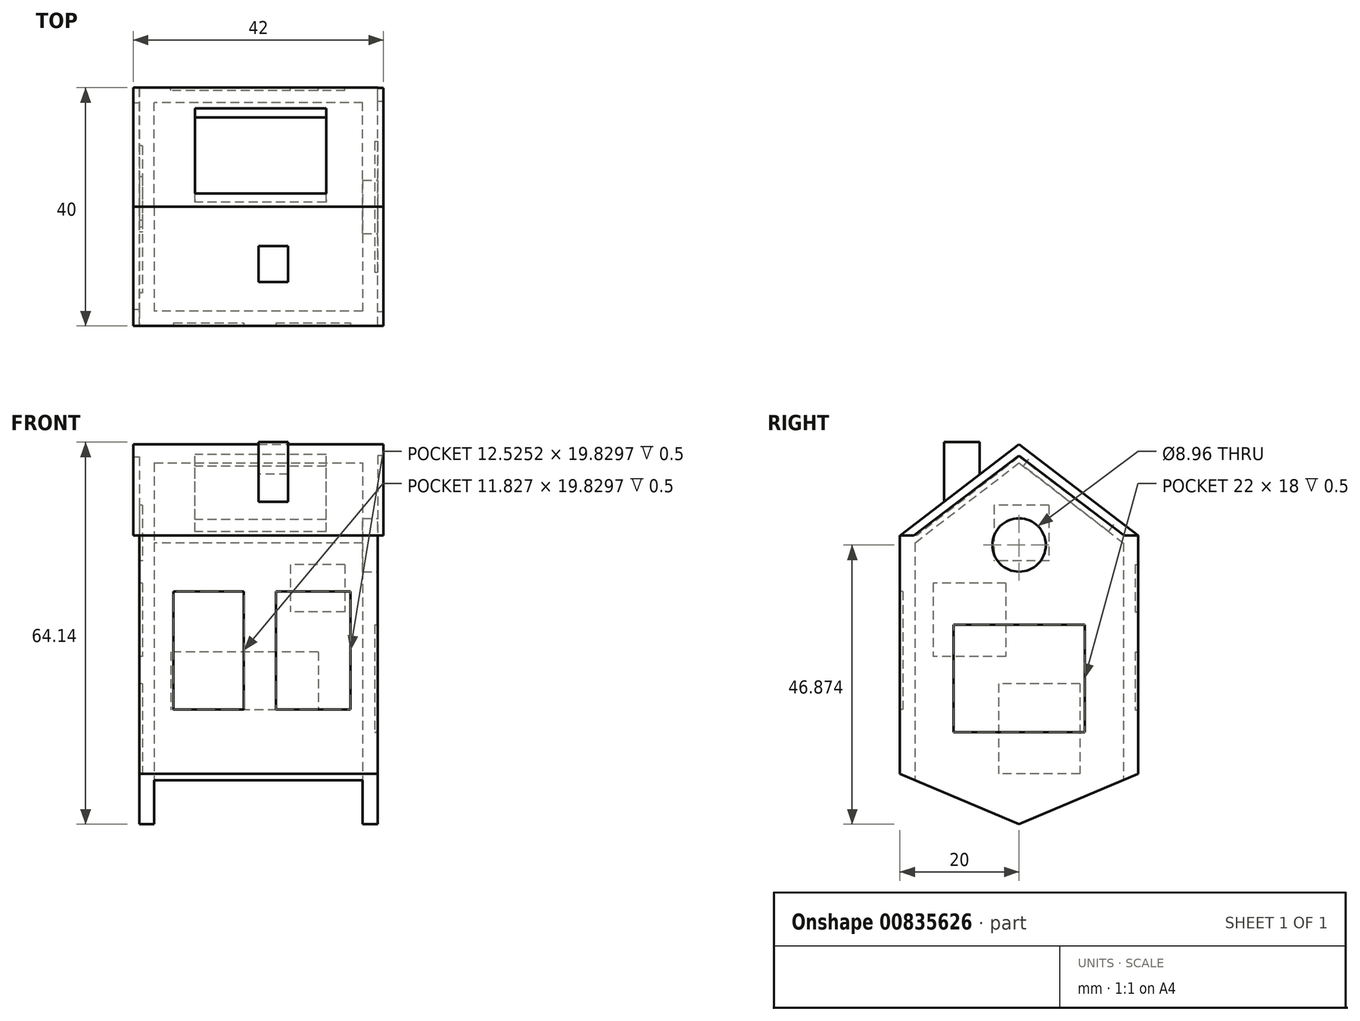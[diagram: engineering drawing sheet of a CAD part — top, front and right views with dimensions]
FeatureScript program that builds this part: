
annotation { "Feature Type Name" : "Feature", "Feature Type Description" : "" }
export const myFeature = defineFeature(function(context is Context, id is Id, definition is map)
    precondition{}
    {
        {
            assignVariable(context, id + "F0", {"name" : "Square", "anyValue" : 40});
        }
        {
            var Q0;
            Q0=qCreatedBy(makeId("Top.planeOp"),FACE);
            var sketch = newSketch(context, id + "F1", { "sketchPlane" : qUnion([Q0])});
            skLineSegment(sketch, "E0.bottom", {"start": v(20, 20) * mm, "end": v(-20, 20) * mm});
            skLineSegment(sketch, "E0.top", {"start": v(20, -20) * mm, "end": v(-20, -20) * mm});
            skLineSegment(sketch, "E0.left", {"start": v(20, 20) * mm, "end": v(20, -20) * mm});
            skLineSegment(sketch, "E0.right", {"start": v(-20, 20) * mm, "end": v(-20, -20) * mm});
            skPoint(sketch, "E0.middle", {"position": v(0, 0) * mm});
            skSolve(sketch);
        }
        {
            var Q0;
            Q0=qSketchRegion(id+"F1",true);
            extrude(context, id + "F2", {"entities" : qUnion([Q0]), "depth" : (getVariable(context, 'Square')) * mm, "offsetDistance" : 25 * mm});
        }
        {
            var Q0;
            Q0=makeQuery(id+"F2.opExtrude","SWEPT_FACE",FACE,{"disambiguationData":[OSD([sQuery(id+"F1.wireOp",EDGE,"E0.left")])]});
            var sketch = newSketch(context, id + "F3", { "sketchPlane" : qUnion([Q0])});
            skLineSegment(sketch, "E1", {"start": v(-20, 0) * mm, "end": v(0, -8.47) * mm});
            skLineSegment(sketch, "E2", {"start": v(0, -8.47) * mm, "end": v(20, 0) * mm});
            skLineSegment(sketch, "E3", {"start": v(-20, 40) * mm, "end": v(0, 55.33) * mm});
            skLineSegment(sketch, "E4", {"start": v(0, 55.33) * mm, "end": v(20, 40) * mm});
            skSolve(sketch);
        }
        {
            var Q0;
            Q0=makeQuery(id+"F2.opExtrude","SWEPT_FACE",FACE,{"disambiguationData":[OSD([sQuery(id+"F1.wireOp",EDGE,"E0.left")])]});
            var sketch = newSketch(context, id + "F4", { "sketchPlane" : qUnion([Q0])});
            skLineSegment(sketch, "E5.bottom", {"start": v(11, 25) * mm, "end": v(-11, 25) * mm});
            skLineSegment(sketch, "E5.top", {"start": v(11, 7) * mm, "end": v(-11, 7) * mm});
            skLineSegment(sketch, "E5.left", {"start": v(11, 25) * mm, "end": v(11, 7) * mm});
            skLineSegment(sketch, "E5.right", {"start": v(-11, 25) * mm, "end": v(-11, 7) * mm});
            skPoint(sketch, "E5.middle", {"position": v(0, 16) * mm});
            skSolve(sketch);
        }
        {
            var Q0;
            Q0=makeQuery(id+"F3.imprint","IMPRINT",FACE,{"disambiguationData":[TD([[makeQuery(id+"F3.imprint","IMPRINT",EDGE,{"derivedFrom":sQuery(id+"F3.wireOp",EDGE,"E3")}),-1.0]])]});
            extrude(context, id + "F5", {"entities" : qUnion([Q0]), "operationType" : NewBodyOperationType.ADD, "depth" : (-getVariable(context, 'Square')) * mm, "offsetDistance" : 25 * mm});
        }
        {
            var Q0;
            Q0=makeQuery(id+"F2.opExtrude","CAP_FACE",FACE,{"disambiguationData":[OSD([sQuery(id+"F1.wireOp",EDGE,"E0.bottom"),sQuery(id+"F1.wireOp",EDGE,"E0.top"),sQuery(id+"F1.wireOp",EDGE,"E0.left"),sQuery(id+"F1.wireOp",EDGE,"E0.right")])],"isStart":true});
            shell(context, id + "F6", {"entities" : qUnion([Q0]), "thickness" : 2.5 * mm});
        }
        {
            var Q0;
            Q0=makeQuery(id+"F4.imprint","IMPRINT",FACE,{"disambiguationData":[TD([[makeQuery(id+"F4.imprint","IMPRINT",EDGE,{"derivedFrom":sQuery(id+"F4.wireOp",EDGE,"E5.bottom")}),1.0]])]});
            extrude(context, id + "F7", {"entities" : qUnion([Q0]), "operationType" : NewBodyOperationType.REMOVE, "oppositeDirection" : true, "depth" : .5 * mm, "offsetDistance" : 25 * mm});
        }
        {
            var Q0;
            Q0=makeQuery(id+"F3.imprint","IMPRINT",FACE,{"disambiguationData":[TD([[makeQuery(id+"F3.imprint","IMPRINT",EDGE,{"derivedFrom":sQuery(id+"F3.wireOp",EDGE,"E1")}),1.0]])]});
            extrude(context, id + "F8", {"entities" : qUnion([Q0]), "operationType" : NewBodyOperationType.ADD, "depth" : (-getVariable(context, 'Square')) * mm, "offsetDistance" : 25 * mm});
        }
        {
            var Q0;
            Q0=qCreatedBy(makeId("Top.planeOp"),FACE);
            var sketch = newSketch(context, id + "F9", { "sketchPlane" : qUnion([Q0])});
            skLineSegment(sketch, "E6.bottom", {"start": v(-20, -20) * mm, "end": v(20, -20) * mm, "construction": true});
            skLineSegment(sketch, "E6.top", {"start": v(-20, 20) * mm, "end": v(20, 20) * mm, "construction": true});
            skLineSegment(sketch, "E6.left", {"start": v(-20, -20) * mm, "end": v(-20, 20) * mm, "construction": true});
            skLineSegment(sketch, "E6.right", {"start": v(20, -20) * mm, "end": v(20, 20) * mm, "construction": true});
            skLineSegment(sketch, "E7.bottom", {"start": v(-17.5, -17.5) * mm, "end": v(17.5, -17.5) * mm});
            skLineSegment(sketch, "E7.top", {"start": v(-17.5, 17.5) * mm, "end": v(17.5, 17.5) * mm});
            skLineSegment(sketch, "E7.left", {"start": v(-17.5, -17.5) * mm, "end": v(-17.5, 17.5) * mm});
            skLineSegment(sketch, "E7.right", {"start": v(17.5, -17.5) * mm, "end": v(17.5, 17.5) * mm});
            skSolve(sketch);
        }
        {
            var Q0;
            Q0=makeQuery(id+"F9.imprint","IMPRINT",FACE,{"disambiguationData":[TD([[makeQuery(id+"F9.imprint","IMPRINT",EDGE,{"derivedFrom":sQuery(id+"F9.wireOp",EDGE,"E7.bottom")}),1.0]])]});
            extrude(context, id + "F10", {"entities" : qUnion([Q0]), "operationType" : NewBodyOperationType.REMOVE, "oppositeDirection" : true, "depth" : 25 * mm, "offsetDistance" : 25 * mm});
        }
        {
            var Q0;
            Q0=makeQuery(id+"F5.opExtrude","SWEPT_FACE",FACE,{"disambiguationData":[OSD([sQuery(id+"F3.wireOp",EDGE,"E4")])]});
            var sketch = newSketch(context, id + "F11", { "sketchPlane" : qUnion([Q0])});
            skLineSegment(sketch, "E8.bottom", {"start": v(11.36, -12.81) * mm, "end": v(-10.64, -12.81) * mm});
            skLineSegment(sketch, "E8.top", {"start": v(11.36, -30.81) * mm, "end": v(-10.64, -30.81) * mm});
            skLineSegment(sketch, "E8.left", {"start": v(11.36, -12.81) * mm, "end": v(11.36, -30.81) * mm});
            skLineSegment(sketch, "E8.right", {"start": v(-10.64, -12.81) * mm, "end": v(-10.64, -30.81) * mm});
            skPoint(sketch, "E8.middle", {"position": v(0.36, -21.81) * mm});
            skSolve(sketch);
        }
        {
            var Q0;
            Q0=makeQuery(id+"F11.imprint","IMPRINT",FACE,{"disambiguationData":[TD([[makeQuery(id+"F11.imprint","IMPRINT",EDGE,{"derivedFrom":sQuery(id+"F11.wireOp",EDGE,"E8.bottom")}),1.0]])]});
            extrude(context, id + "F12", {"entities" : qUnion([Q0]), "operationType" : NewBodyOperationType.REMOVE, "depth" : -2.5 * mm, "offsetDistance" : 25 * mm});
        }
        {
            var Q0;
            Q0=qCreatedBy(makeId("Right.planeOp"),FACE);
            var sketch = newSketch(context, id + "F13", { "sketchPlane" : qUnion([Q0])});
            skLineSegment(sketch, "E9.bottom", {"start": v(-6.6, 45.02) * mm, "end": v(-12.6, 45.02) * mm});
            skLineSegment(sketch, "E9.top", {"start": v(-6.6, 55.67) * mm, "end": v(-12.6, 55.67) * mm});
            skLineSegment(sketch, "E9.left", {"start": v(-6.6, 45.02) * mm, "end": v(-6.6, 55.67) * mm});
            skLineSegment(sketch, "E9.right", {"start": v(-12.6, 45.02) * mm, "end": v(-12.6, 55.67) * mm});
            skSolve(sketch);
        }
        {
            var Q0;
            Q0=makeQuery(id+"F13.imprint","IMPRINT",FACE,{"disambiguationData":[TD([[makeQuery(id+"F13.imprint","IMPRINT",EDGE,{"derivedFrom":sQuery(id+"F13.wireOp",EDGE,"E9.bottom")}),-1.0]])]});
            extrude(context, id + "F14", {"entities" : qUnion([Q0]), "operationType" : NewBodyOperationType.ADD, "depth" : 5 * mm, "offsetDistance" : 25 * mm});
        }
        {
            var Q0;
            {var subQ0=sQuery(id+"F13.wireOp",EDGE,"E9.bottom");var subQ1=sQuery(id+"F13.wireOp",EDGE,"E9.left");Q0=makeQuery(id+"F14.boolean.opBoolean","SPLIT",FACE,{"disambiguationData":[TD([makeQuery(id+"F6.opShell","OFFSET_FACE",FACE,{"disambiguationData":[OSD([sQuery(id+"F3.wireOp",EDGE,"E3")])]})])],"derivedFrom":makeQuery(id+"F14.opExtrude","CAP_FACE",FACE,{"disambiguationData":[OSD([subQ0,sQuery(id+"F13.wireOp",EDGE,"E9.top"),subQ1,sQuery(id+"F13.wireOp",EDGE,"E9.right")])],"isStart":false})});}
            extrude(context, id + "F15", {"entities" : qUnion([Q0]), "operationType" : NewBodyOperationType.REMOVE, "oppositeDirection" : true, "depth" : 5 * mm, "offsetDistance" : 25 * mm});
        }
        {
            var Q0;
            Q0=makeQuery(id+"F3.imprint","IMPRINT",FACE,{"disambiguationData":[TD([[makeQuery(id+"F3.imprint","IMPRINT",EDGE,{"derivedFrom":sQuery(id+"F3.wireOp",EDGE,"E3")}),-1.0]])]});
            var sketch = newSketch(context, id + "F16", { "sketchPlane" : qUnion([Q0])});
            skLineSegment(sketch, "E10", {"start": v(-20.18, 40.03) * mm, "end": v(-17.67, 40.03) * mm});
            skLineSegment(sketch, "E11", {"start": v(-17.67, 40.03) * mm, "end": v(0, 53.43) * mm});
            skLineSegment(sketch, "E12", {"start": v(0, 53.43) * mm, "end": v(17.64, 40.03) * mm});
            skLineSegment(sketch, "E13", {"start": v(17.64, 40.03) * mm, "end": v(20.18, 40.03) * mm});
            skCircle(sketch, "E14", {"center": v(0, 38.4) * mm, "radius": 4.48 * mm});
            skSolve(sketch);
        }
        {
            var Q0;
            {var subQ4=sQuery(id+"F16.wireOp",EDGE,"E11");Q0=makeQuery(id+"F16.imprint","IMPRINT",FACE,{"disambiguationData":[TD([[makeQuery(id+"F16.imprint","IMPRINT",EDGE,{"derivedFrom":subQ4}),1.0]])]});}
            extrude(context, id + "F17", {"entities" : qUnion([Q0]), "operationType" : NewBodyOperationType.ADD, "depth" : 1 * mm, "offsetDistance" : 25 * mm});
        }
        {
            var Q0;
            {var subQ0=sQuery(id+"F1.wireOp",EDGE,"E0.left");Q0=makeQuery(id+"F8.boolean.opBoolean","MERGE",FACE,{"derivedFrom":[makeQuery(id+"F5.boolean.opBoolean","MERGE",FACE,{"derivedFrom":[makeQuery(id+"F2.opExtrude","SWEPT_FACE",FACE,{"disambiguationData":[OSD([sQuery(id+"F1.wireOp",EDGE,"E0.right")])]}),makeQuery(id+"F5.opExtrude","CAP_FACE",FACE,{"disambiguationData":[OSD([subQ0,sQuery(id+"F3.wireOp",EDGE,"E3"),sQuery(id+"F3.wireOp",EDGE,"E4")])],"isStart":false})]}),makeQuery(id+"F8.opExtrude","CAP_FACE",FACE,{"disambiguationData":[OSD([subQ0,sQuery(id+"F3.wireOp",EDGE,"E1"),sQuery(id+"F3.wireOp",EDGE,"E2")])],"isStart":false})]});}
            var sketch = newSketch(context, id + "F18", { "sketchPlane" : qUnion([Q0])});
            skLineSegment(sketch, "E15", {"start": v(-20, 40) * mm, "end": v(-17.5, 40) * mm});
            skLineSegment(sketch, "E16", {"start": v(-17.5, 40) * mm, "end": v(0, 53.18) * mm});
            skLineSegment(sketch, "E17", {"start": v(0, 53.18) * mm, "end": v(17.2, 40) * mm});
            skLineSegment(sketch, "E18", {"start": v(17.2, 40) * mm, "end": v(20, 40) * mm});
            skLineSegment(sketch, "E19.bottom", {"start": v(-5.02, 45.07) * mm, "end": v(4.21, 45.07) * mm});
            skLineSegment(sketch, "E19.top", {"start": v(-5.02, 35.76) * mm, "end": v(4.21, 35.76) * mm});
            skLineSegment(sketch, "E19.left", {"start": v(-5.02, 45.07) * mm, "end": v(-5.02, 35.76) * mm});
            skLineSegment(sketch, "E19.right", {"start": v(4.21, 45.07) * mm, "end": v(4.21, 35.76) * mm});
            skLineSegment(sketch, "E20.bottom", {"start": v(2.24, 32) * mm, "end": v(14.45, 32) * mm});
            skLineSegment(sketch, "E20.top", {"start": v(2.24, 19.7) * mm, "end": v(14.45, 19.7) * mm});
            skLineSegment(sketch, "E20.left", {"start": v(2.24, 32) * mm, "end": v(2.24, 19.7) * mm});
            skLineSegment(sketch, "E20.right", {"start": v(14.45, 32) * mm, "end": v(14.45, 19.7) * mm});
            skLineSegment(sketch, "E21.bottom", {"start": v(-10.23, 15.12) * mm, "end": v(3.44, 15.12) * mm});
            skLineSegment(sketch, "E21.top", {"start": v(-10.23, 0) * mm, "end": v(3.44, 0) * mm});
            skLineSegment(sketch, "E21.left", {"start": v(-10.23, 15.12) * mm, "end": v(-10.23, 0) * mm});
            skLineSegment(sketch, "E21.right", {"start": v(3.44, 15.12) * mm, "end": v(3.44, 0) * mm});
            skSolve(sketch);
        }
        {
            var Q0;
            Q0 = qSketchRegion(id + "F18", true);
            extrude(context, id + "F19", {"entities" : qUnion([Q0]), "operationType" : NewBodyOperationType.REMOVE, "depth" : -.5 * mm, "offsetDistance" : 25 * mm});
        }
        {
            var Q0;
            Q0=makeQuery(id+"F18.imprint","IMPRINT",FACE,{"disambiguationData":[TD([[makeQuery(id+"F18.imprint","IMPRINT",EDGE,{"derivedFrom":sQuery(id+"F18.wireOp",EDGE,"E15")}),1.0]])]});
            extrude(context, id + "F20", {"entities" : qUnion([Q0]), "operationType" : NewBodyOperationType.ADD, "depth" : 1 * mm, "offsetDistance" : 25 * mm});
        }
        {
            var Q0;
            Q0=makeQuery(id+"F2.opExtrude","SWEPT_FACE",FACE,{"disambiguationData":[OSD([sQuery(id+"F1.wireOp",EDGE,"E0.bottom")])]});
            var sketch = newSketch(context, id + "F21", { "sketchPlane" : qUnion([Q0])});
            skLineSegment(sketch, "E22.bottom", {"start": v(-14.52, 35.1) * mm, "end": v(-5.33, 35.1) * mm});
            skLineSegment(sketch, "E22.top", {"start": v(-14.52, 27.17) * mm, "end": v(-5.33, 27.17) * mm});
            skLineSegment(sketch, "E22.left", {"start": v(-14.52, 35.1) * mm, "end": v(-14.52, 27.17) * mm});
            skLineSegment(sketch, "E22.right", {"start": v(-5.33, 35.1) * mm, "end": v(-5.33, 27.17) * mm});
            skLineSegment(sketch, "E23.bottom", {"start": v(-10.03, 20.47) * mm, "end": v(14.7, 20.47) * mm});
            skLineSegment(sketch, "E23.top", {"start": v(-10.03, 10.75) * mm, "end": v(14.7, 10.75) * mm});
            skLineSegment(sketch, "E23.left", {"start": v(-10.03, 20.47) * mm, "end": v(-10.03, 10.75) * mm});
            skLineSegment(sketch, "E23.right", {"start": v(14.7, 20.47) * mm, "end": v(14.7, 10.75) * mm});
            skSolve(sketch);
        }
        {
            var Q0;
            Q0=makeQuery(id+"F21.imprint","IMPRINT",FACE,{"disambiguationData":[TD([[makeQuery(id+"F21.imprint","IMPRINT",EDGE,{"derivedFrom":sQuery(id+"F21.wireOp",EDGE,"E22.bottom")}),-1.0]])]});
            var Q1;
            Q1=makeQuery(id+"F21.imprint","IMPRINT",FACE,{"disambiguationData":[TD([[makeQuery(id+"F21.imprint","IMPRINT",EDGE,{"derivedFrom":sQuery(id+"F21.wireOp",EDGE,"E23.bottom")}),-1.0]])]});
            extrude(context, id + "F22", {"entities" : qUnion([Q0, Q1]), "operationType" : NewBodyOperationType.REMOVE, "oppositeDirection" : true, "depth" : .5 * mm, "offsetDistance" : 25 * mm});
        }
        {
            var Q0;
            Q0=makeQuery(id+"F2.opExtrude","SWEPT_FACE",FACE,{"disambiguationData":[OSD([sQuery(id+"F1.wireOp",EDGE,"E0.top")])]});
            var sketch = newSketch(context, id + "F23", { "sketchPlane" : qUnion([Q0])});
            skLineSegment(sketch, "E24.bottom", {"start": v(-14.25, 30.63) * mm, "end": v(-2.42, 30.63) * mm});
            skLineSegment(sketch, "E24.top", {"start": v(-14.25, 10.8) * mm, "end": v(-2.42, 10.8) * mm});
            skLineSegment(sketch, "E24.left", {"start": v(-14.25, 30.63) * mm, "end": v(-14.25, 10.8) * mm});
            skLineSegment(sketch, "E24.right", {"start": v(-2.42, 30.63) * mm, "end": v(-2.42, 10.8) * mm});
            skLineSegment(sketch, "E25.bottom", {"start": v(2.93, 30.63) * mm, "end": v(15.45, 30.63) * mm});
            skLineSegment(sketch, "E25.top", {"start": v(2.93, 10.8) * mm, "end": v(15.45, 10.8) * mm});
            skLineSegment(sketch, "E25.left", {"start": v(2.93, 30.63) * mm, "end": v(2.93, 10.8) * mm});
            skLineSegment(sketch, "E25.right", {"start": v(15.45, 30.63) * mm, "end": v(15.45, 10.8) * mm});
            skSolve(sketch);
        }
        {
            var Q0;
            Q0=makeQuery(id+"F23.imprint","IMPRINT",FACE,{"disambiguationData":[TD([[makeQuery(id+"F23.imprint","IMPRINT",EDGE,{"derivedFrom":sQuery(id+"F23.wireOp",EDGE,"E24.bottom")}),-1.0]])]});
            var Q1;
            Q1=makeQuery(id+"F23.imprint","IMPRINT",FACE,{"disambiguationData":[TD([[makeQuery(id+"F23.imprint","IMPRINT",EDGE,{"derivedFrom":sQuery(id+"F23.wireOp",EDGE,"E25.bottom")}),-1.0]])]});
            extrude(context, id + "F24", {"entities" : qUnion([Q0, Q1]), "operationType" : NewBodyOperationType.REMOVE, "oppositeDirection" : true, "depth" : .5 * mm, "offsetDistance" : 25 * mm});
        }
        {
            var Q0;
            Q0 = qSketchRegion(id + "F16", true);
            extrude(context, id + "F25", {"entities" : qUnion([Q0]), "operationType" : NewBodyOperationType.REMOVE, "oppositeDirection" : true, "depth" : 2.5 * mm, "offsetDistance" : 25 * mm});
        }
    });
